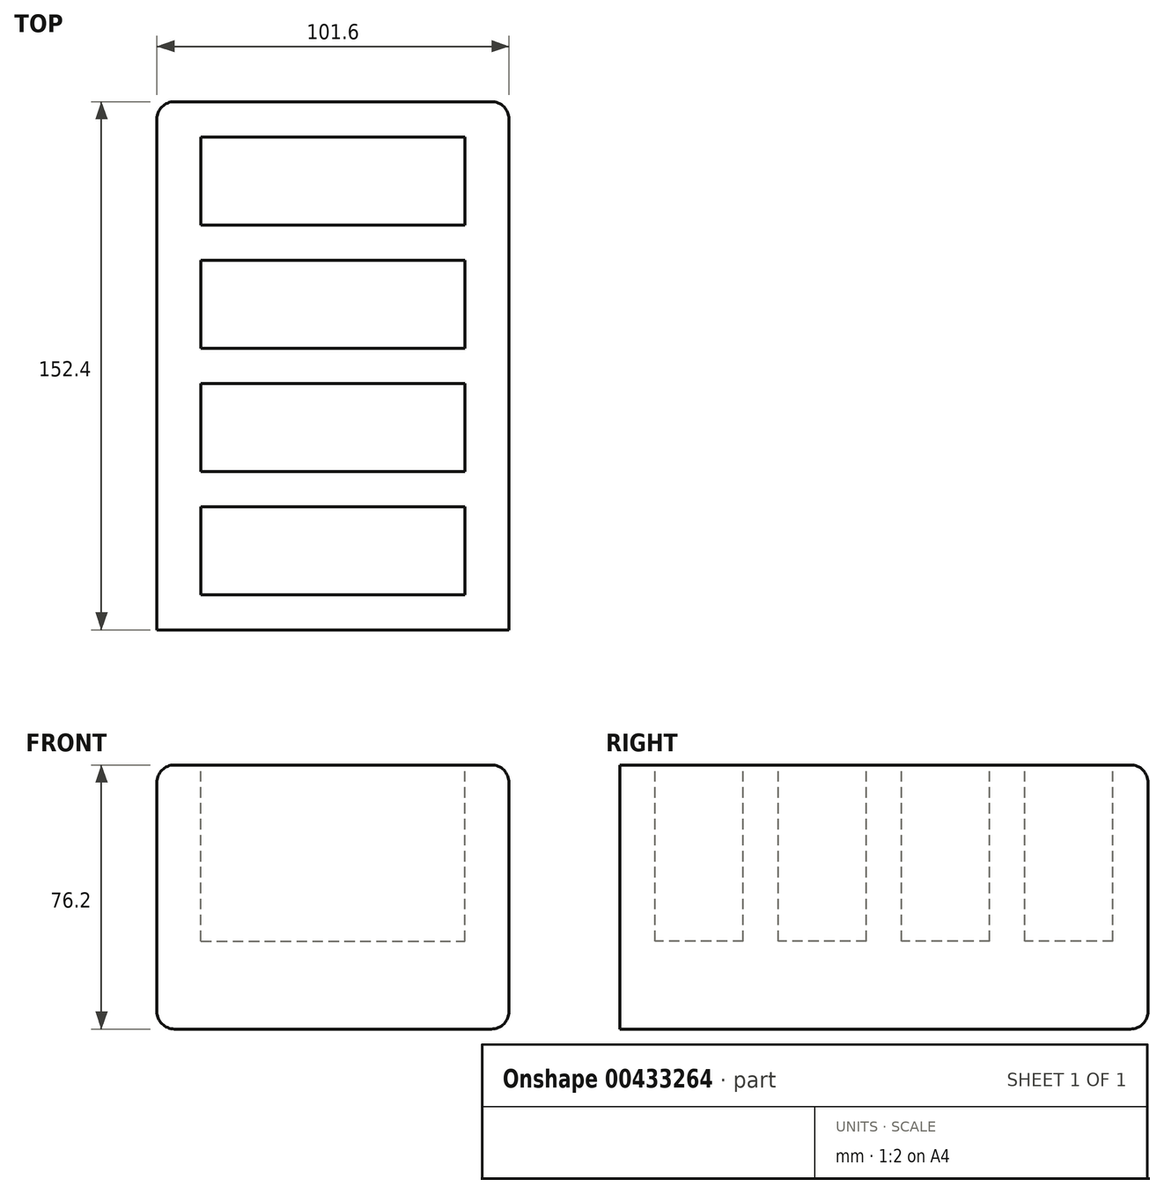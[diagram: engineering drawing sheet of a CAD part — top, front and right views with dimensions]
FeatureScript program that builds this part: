
annotation { "Feature Type Name" : "Feature", "Feature Type Description" : "" }
export const myFeature = defineFeature(function(context is Context, id is Id, definition is map)
    precondition{}
    {
        {
            var Q0;
            Q0=qCreatedBy(makeId("Top.planeOp"),FACE);
            var sketch = newSketch(context, id + "F0", { "sketchPlane" : qUnion([Q0])});
            skLineSegment(sketch, "E0.bottom", {"start": v(50.8, -76.2) * mm, "end": v(-50.8, -76.2) * mm});
            skLineSegment(sketch, "E0.top", {"start": v(50.8, 76.2) * mm, "end": v(-50.8, 76.2) * mm});
            skLineSegment(sketch, "E0.left", {"start": v(50.8, -76.2) * mm, "end": v(50.8, 76.2) * mm});
            skLineSegment(sketch, "E0.right", {"start": v(-50.8, -76.2) * mm, "end": v(-50.8, 76.2) * mm});
            skPoint(sketch, "E0.middle", {"position": v(0, 0) * mm});
            skSolve(sketch);
        }
        {
            var Q0;
            Q0 = qSketchRegion(id + "F0", true);
            extrude(context, id + "F1", {"entities" : qUnion([Q0]), "depth" : 76.2 * mm});
        }
        {
            var Q0;
            Q0=makeQuery(id+"F1.opExtrude","CAP_FACE",FACE,{"disambiguationData":[OSD([sQuery(id+"F0.wireOp",EDGE,"E0.bottom"),sQuery(id+"F0.wireOp",EDGE,"E0.top"),sQuery(id+"F0.wireOp",EDGE,"E0.left"),sQuery(id+"F0.wireOp",EDGE,"E0.right")])],"isStart":false});
            var sketch = newSketch(context, id + "F2", { "sketchPlane" : qUnion([Q0])});
            skLineSegment(sketch, "E1.bottom", {"start": v(-38.1, 66.04) * mm, "end": v(38.1, 66.04) * mm});
            skLineSegment(sketch, "E1.top", {"start": v(-38.1, 40.64) * mm, "end": v(38.1, 40.64) * mm});
            skLineSegment(sketch, "E1.left", {"start": v(-38.1, 66.04) * mm, "end": v(-38.1, 40.64) * mm});
            skLineSegment(sketch, "E1.right", {"start": v(38.1, 66.04) * mm, "end": v(38.1, 40.64) * mm});
            skLineSegment(sketch, "E2.0.1.0", {"start": v(-38.1, 30.48) * mm, "end": v(-38.1, 5.08) * mm});
            skLineSegment(sketch, "E2.0.1.1", {"start": v(-38.1, 30.48) * mm, "end": v(38.1, 30.48) * mm});
            skLineSegment(sketch, "E2.0.1.2", {"start": v(38.1, 30.48) * mm, "end": v(38.1, 5.08) * mm});
            skLineSegment(sketch, "E2.0.1.3", {"start": v(-38.1, 5.08) * mm, "end": v(38.1, 5.08) * mm});
            skLineSegment(sketch, "E2.0.2.0", {"start": v(-38.1, -5.08) * mm, "end": v(-38.1, -30.48) * mm});
            skLineSegment(sketch, "E2.0.2.1", {"start": v(-38.1, -5.08) * mm, "end": v(38.1, -5.08) * mm});
            skLineSegment(sketch, "E2.0.2.2", {"start": v(38.1, -5.08) * mm, "end": v(38.1, -30.48) * mm});
            skLineSegment(sketch, "E2.0.2.3", {"start": v(-38.1, -30.48) * mm, "end": v(38.1, -30.48) * mm});
            skLineSegment(sketch, "E2.0.3.0", {"start": v(-38.1, -40.64) * mm, "end": v(-38.1, -66.04) * mm});
            skLineSegment(sketch, "E2.0.3.1", {"start": v(-38.1, -40.64) * mm, "end": v(38.1, -40.64) * mm});
            skLineSegment(sketch, "E2.0.3.2", {"start": v(38.1, -40.64) * mm, "end": v(38.1, -66.04) * mm});
            skLineSegment(sketch, "E2.0.3.3", {"start": v(-38.1, -66.04) * mm, "end": v(38.1, -66.04) * mm});
            skLineSegment(sketch, "E2.direction1", {"start": v(-38.1, 40.64) * mm, "end": v(-12.7, 40.64) * mm, "construction": true});
            skLineSegment(sketch, "E2.direction2", {"start": v(-38.1, 40.64) * mm, "end": v(-38.1, 5.08) * mm, "construction": true});
            skSolve(sketch);
        }
        {
            var Q0;
            Q0=makeQuery(id+"F2.imprint","IMPRINT",FACE,{"disambiguationData":[TD([[makeQuery(id+"F2.imprint","IMPRINT",EDGE,{"derivedFrom":sQuery(id+"F2.wireOp",EDGE,"E1.bottom")}),-1.0]])]});
            var Q1;
            Q1=makeQuery(id+"F2.imprint","IMPRINT",FACE,{"disambiguationData":[TD([[makeQuery(id+"F2.imprint","IMPRINT",EDGE,{"derivedFrom":sQuery(id+"F2.wireOp",EDGE,"E2.0.1.0")}),1.0]])]});
            var Q2;
            Q2=makeQuery(id+"F2.imprint","IMPRINT",FACE,{"disambiguationData":[TD([[makeQuery(id+"F2.imprint","IMPRINT",EDGE,{"derivedFrom":sQuery(id+"F2.wireOp",EDGE,"E2.0.2.0")}),1.0]])]});
            var Q3;
            Q3=makeQuery(id+"F2.imprint","IMPRINT",FACE,{"disambiguationData":[TD([[makeQuery(id+"F2.imprint","IMPRINT",EDGE,{"derivedFrom":sQuery(id+"F2.wireOp",EDGE,"E2.0.3.0")}),1.0]])]});
            extrude(context, id + "F3", {"entities" : qUnion([Q0, Q1, Q2, Q3]), "operationType" : NewBodyOperationType.REMOVE, "oppositeDirection" : true, "depth" : 50.8 * mm});
        }
        {
            var Q0;
            Q0=makeQuery(id+"F1.opExtrude","SWEPT_EDGE",EDGE,{"disambiguationData":[OSD([sQuery(id+"F0.wireOp",EDGE,"E0.top"),sQuery(id+"F0.wireOp",EDGE,"E0.right")])]});
            var Q1;
            Q1=makeQuery(id+"F1.opExtrude","SWEPT_EDGE",EDGE,{"disambiguationData":[OSD([sQuery(id+"F0.wireOp",EDGE,"E0.top"),sQuery(id+"F0.wireOp",EDGE,"E0.left")])]});
            var Q2;
            Q2=makeQuery(id+"F1.opExtrude","CAP_EDGE",EDGE,{"disambiguationData":[OSD([sQuery(id+"F0.wireOp",EDGE,"E0.left")])],"isStart":false});
            var Q3;
            Q3=makeQuery(id+"F1.opExtrude","CAP_EDGE",EDGE,{"disambiguationData":[OSD([sQuery(id+"F0.wireOp",EDGE,"E0.top")])],"isStart":false});
            var Q4;
            Q4=makeQuery(id+"F1.opExtrude","SWEPT_FACE",FACE,{"disambiguationData":[OSD([sQuery(id+"F0.wireOp",EDGE,"E0.top")])]});
            var Q5;
            Q5=makeQuery(id+"F1.opExtrude","CAP_EDGE",EDGE,{"disambiguationData":[OSD([sQuery(id+"F0.wireOp",EDGE,"E0.right")])],"isStart":true});
            var Q6;
            Q6=makeQuery(id+"F1.opExtrude","CAP_EDGE",EDGE,{"disambiguationData":[OSD([sQuery(id+"F0.wireOp",EDGE,"E0.left")])],"isStart":true});
            var Q7;
            Q7=makeQuery(id+"F1.opExtrude","CAP_EDGE",EDGE,{"disambiguationData":[OSD([sQuery(id+"F0.wireOp",EDGE,"E0.right")])],"isStart":false});
            fillet(context, id + "F4", {"entities" : qUnion([Q0, Q1, Q2, Q3, Q4, Q5, Q6, Q7]), "radius" : 5.08 * mm, "tangentPropagation" : true, "allowEdgeOverflow" : false});
        }
    });
